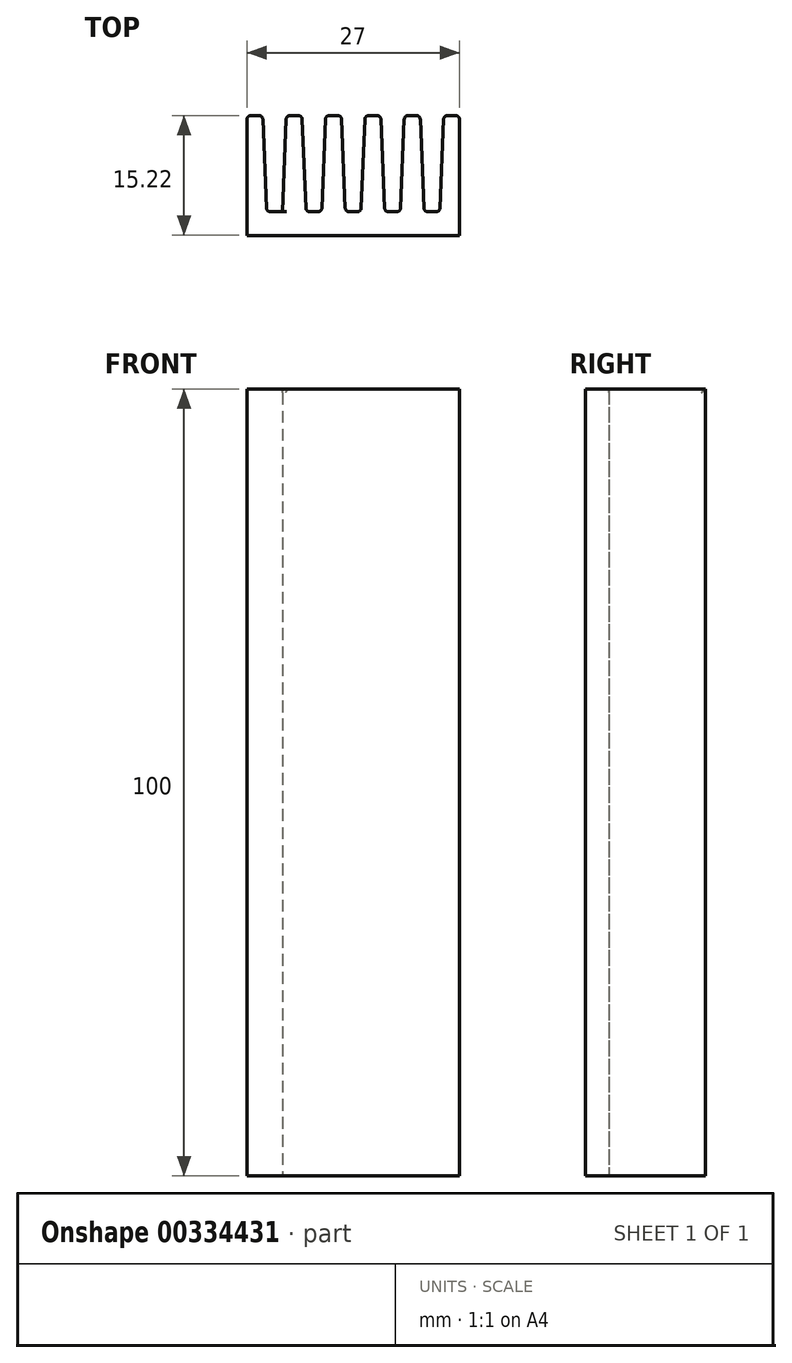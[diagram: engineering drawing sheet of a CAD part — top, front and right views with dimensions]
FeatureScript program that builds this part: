
annotation { "Feature Type Name" : "Feature", "Feature Type Description" : "" }
export const myFeature = defineFeature(function(context is Context, id is Id, definition is map)
    precondition{}
    {
        {
            var Q0;
            Q0=qCreatedBy(makeId("Top.planeOp"),FACE);
            var sketch = newSketch(context, id + "F0", { "sketchPlane" : qUnion([Q0])});
            skLineSegment(sketch, "E0", {"start": v(-38.74, 8.35) * mm, "end": v(-38.74, -6.87) * mm});
            skLineSegment(sketch, "E1", {"start": v(-38.74, 8.35) * mm, "end": v(-36.74, 8.35) * mm});
            skLineSegment(sketch, "E2", {"start": v(-36.74, 8.35) * mm, "end": v(-36.24, -3.87) * mm});
            skLineSegment(sketch, "E3", {"start": v(-36.24, -3.87) * mm, "end": v(-34.24, -3.87) * mm});
            skLineSegment(sketch, "E4", {"start": v(-34.24, -3.87) * mm, "end": v(-33.74, 8.35) * mm});
            skLineSegment(sketch, "E5", {"start": v(-33.74, 8.35) * mm, "end": v(-31.74, 8.35) * mm});
            skLineSegment(sketch, "E6.1.0.0", {"start": v(-28.74, 8.35) * mm, "end": v(-26.74, 8.35) * mm});
            skLineSegment(sketch, "E6.1.0.1", {"start": v(-29.24, -3.87) * mm, "end": v(-28.74, 8.35) * mm});
            skLineSegment(sketch, "E6.1.0.2", {"start": v(-31.24, -3.87) * mm, "end": v(-29.24, -3.87) * mm});
            skLineSegment(sketch, "E6.1.0.3", {"start": v(-31.74, 8.35) * mm, "end": v(-31.24, -3.87) * mm});
            skLineSegment(sketch, "E6.2.0.0", {"start": v(-23.74, 8.35) * mm, "end": v(-21.74, 8.35) * mm});
            skLineSegment(sketch, "E6.2.0.1", {"start": v(-24.24, -3.87) * mm, "end": v(-23.74, 8.35) * mm});
            skLineSegment(sketch, "E6.2.0.2", {"start": v(-26.24, -3.87) * mm, "end": v(-24.24, -3.87) * mm});
            skLineSegment(sketch, "E6.2.0.3", {"start": v(-26.74, 8.35) * mm, "end": v(-26.24, -3.87) * mm});
            skLineSegment(sketch, "E6.3.0.0", {"start": v(-18.74, 8.35) * mm, "end": v(-16.74, 8.35) * mm});
            skLineSegment(sketch, "E6.3.0.1", {"start": v(-19.24, -3.87) * mm, "end": v(-18.74, 8.35) * mm});
            skLineSegment(sketch, "E6.3.0.2", {"start": v(-21.24, -3.87) * mm, "end": v(-19.24, -3.87) * mm});
            skLineSegment(sketch, "E6.3.0.3", {"start": v(-21.74, 8.35) * mm, "end": v(-21.24, -3.87) * mm});
            skLineSegment(sketch, "E6.4.0.0", {"start": v(-13.74, 8.35) * mm, "end": v(-11.74, 8.35) * mm});
            skLineSegment(sketch, "E6.4.0.1", {"start": v(-14.24, -3.87) * mm, "end": v(-13.74, 8.35) * mm});
            skLineSegment(sketch, "E6.4.0.2", {"start": v(-16.24, -3.87) * mm, "end": v(-14.24, -3.87) * mm});
            skLineSegment(sketch, "E6.4.0.3", {"start": v(-16.74, 8.35) * mm, "end": v(-16.24, -3.87) * mm});
            skLineSegment(sketch, "E6.direction1", {"start": v(-36.24, -3.87) * mm, "end": v(-31.24, -3.87) * mm, "construction": true});
            skLineSegment(sketch, "E7", {"start": v(-11.74, 8.35) * mm, "end": v(-11.74, -6.87) * mm});
            skLineSegment(sketch, "E8", {"start": v(-11.74, -6.87) * mm, "end": v(-38.74, -6.87) * mm});
            skSolve(sketch);
        }
        {
            var Q0;
            Q0=makeQuery(id+"F0.imprint","IMPRINT",FACE,{"disambiguationData":[TD([[makeQuery(id+"F0.imprint","IMPRINT",EDGE,{"derivedFrom":sQuery(id+"F0.wireOp",EDGE,"E0")}),1.0]])]});
            extrude(context, id + "F1", {"entities" : qUnion([Q0]), "depth" : 100 * mm});
        }
        {
            var Q0;
            Q0=makeQuery(id+"F1.opExtrude","SWEPT_EDGE",EDGE,{"disambiguationData":[OSD([sQuery(id+"F0.wireOp",EDGE,"E6.4.0.0"),sQuery(id+"F0.wireOp",EDGE,"E6.4.0.1")])]});
            var Q1;
            Q1=makeQuery(id+"F1.opExtrude","SWEPT_EDGE",EDGE,{"disambiguationData":[OSD([sQuery(id+"F0.wireOp",EDGE,"E6.4.0.0"),sQuery(id+"F0.wireOp",EDGE,"E7")])]});
            var Q2;
            Q2=makeQuery(id+"F1.opExtrude","SWEPT_EDGE",EDGE,{"disambiguationData":[OSD([sQuery(id+"F0.wireOp",EDGE,"E6.3.0.0"),sQuery(id+"F0.wireOp",EDGE,"E6.3.0.1")])]});
            var Q3;
            Q3=makeQuery(id+"F1.opExtrude","SWEPT_EDGE",EDGE,{"disambiguationData":[OSD([sQuery(id+"F0.wireOp",EDGE,"E6.3.0.0"),sQuery(id+"F0.wireOp",EDGE,"E6.4.0.3")])]});
            var Q4;
            Q4=makeQuery(id+"F1.opExtrude","SWEPT_EDGE",EDGE,{"disambiguationData":[OSD([sQuery(id+"F0.wireOp",EDGE,"E6.2.0.0"),sQuery(id+"F0.wireOp",EDGE,"E6.2.0.1")])]});
            var Q5;
            Q5=makeQuery(id+"F1.opExtrude","SWEPT_EDGE",EDGE,{"disambiguationData":[OSD([sQuery(id+"F0.wireOp",EDGE,"E6.2.0.0"),sQuery(id+"F0.wireOp",EDGE,"E6.3.0.3")])]});
            var Q6;
            Q6=makeQuery(id+"F1.opExtrude","SWEPT_EDGE",EDGE,{"disambiguationData":[OSD([sQuery(id+"F0.wireOp",EDGE,"E6.1.0.0"),sQuery(id+"F0.wireOp",EDGE,"E6.1.0.1")])]});
            var Q7;
            Q7=makeQuery(id+"F1.opExtrude","SWEPT_EDGE",EDGE,{"disambiguationData":[OSD([sQuery(id+"F0.wireOp",EDGE,"E6.1.0.0"),sQuery(id+"F0.wireOp",EDGE,"E6.2.0.3")])]});
            var Q8;
            Q8=makeQuery(id+"F1.opExtrude","SWEPT_EDGE",EDGE,{"disambiguationData":[OSD([sQuery(id+"F0.wireOp",EDGE,"E4"),sQuery(id+"F0.wireOp",EDGE,"E5")])]});
            var Q9;
            Q9=makeQuery(id+"F1.opExtrude","SWEPT_EDGE",EDGE,{"disambiguationData":[OSD([sQuery(id+"F0.wireOp",EDGE,"E5"),sQuery(id+"F0.wireOp",EDGE,"E6.1.0.3")])]});
            var Q10;
            Q10=makeQuery(id+"F1.opExtrude","SWEPT_EDGE",EDGE,{"disambiguationData":[OSD([sQuery(id+"F0.wireOp",EDGE,"E0"),sQuery(id+"F0.wireOp",EDGE,"E1")])]});
            var Q11;
            Q11=makeQuery(id+"F1.opExtrude","SWEPT_EDGE",EDGE,{"disambiguationData":[OSD([sQuery(id+"F0.wireOp",EDGE,"E1"),sQuery(id+"F0.wireOp",EDGE,"E2")])]});
            var Q12;
            Q12=makeQuery(id+"F1.opExtrude","SWEPT_EDGE",EDGE,{"disambiguationData":[OSD([sQuery(id+"F0.wireOp",EDGE,"E2"),sQuery(id+"F0.wireOp",EDGE,"E3")])]});
            var Q13;
            Q13=makeQuery(id+"F1.opExtrude","CAP_EDGE",EDGE,{"disambiguationData":[OSD([sQuery(id+"F0.wireOp",EDGE,"E4")])],"isStart":false});
            var Q14;
            Q14=makeQuery(id+"F1.opExtrude","SWEPT_EDGE",EDGE,{"disambiguationData":[OSD([sQuery(id+"F0.wireOp",EDGE,"E6.1.0.2"),sQuery(id+"F0.wireOp",EDGE,"E6.1.0.3")])]});
            var Q15;
            Q15=makeQuery(id+"F1.opExtrude","SWEPT_EDGE",EDGE,{"disambiguationData":[OSD([sQuery(id+"F0.wireOp",EDGE,"E6.2.0.2"),sQuery(id+"F0.wireOp",EDGE,"E6.2.0.3")])]});
            var Q16;
            Q16=makeQuery(id+"F1.opExtrude","SWEPT_EDGE",EDGE,{"disambiguationData":[OSD([sQuery(id+"F0.wireOp",EDGE,"E6.2.0.1"),sQuery(id+"F0.wireOp",EDGE,"E6.2.0.2")])]});
            var Q17;
            Q17=makeQuery(id+"F1.opExtrude","SWEPT_EDGE",EDGE,{"disambiguationData":[OSD([sQuery(id+"F0.wireOp",EDGE,"E6.1.0.1"),sQuery(id+"F0.wireOp",EDGE,"E6.1.0.2")])]});
            var Q18;
            Q18=makeQuery(id+"F1.opExtrude","SWEPT_EDGE",EDGE,{"disambiguationData":[OSD([sQuery(id+"F0.wireOp",EDGE,"E6.3.0.2"),sQuery(id+"F0.wireOp",EDGE,"E6.3.0.3")])]});
            var Q19;
            Q19=makeQuery(id+"F1.opExtrude","SWEPT_EDGE",EDGE,{"disambiguationData":[OSD([sQuery(id+"F0.wireOp",EDGE,"E6.3.0.1"),sQuery(id+"F0.wireOp",EDGE,"E6.3.0.2")])]});
            var Q20;
            Q20=makeQuery(id+"F1.opExtrude","SWEPT_EDGE",EDGE,{"disambiguationData":[OSD([sQuery(id+"F0.wireOp",EDGE,"E6.4.0.2"),sQuery(id+"F0.wireOp",EDGE,"E6.4.0.3")])]});
            var Q21;
            Q21=makeQuery(id+"F1.opExtrude","SWEPT_EDGE",EDGE,{"disambiguationData":[OSD([sQuery(id+"F0.wireOp",EDGE,"E6.4.0.1"),sQuery(id+"F0.wireOp",EDGE,"E6.4.0.2")])]});
            fillet(context, id + "F2", {"entities" : qUnion([Q0, Q1, Q2, Q3, Q4, Q5, Q6, Q7, Q8, Q9, Q10, Q11, Q12, Q13, Q14, Q15, Q16, Q17, Q18, Q19, Q20, Q21]), "radius" : 0.5 * mm, "tangentPropagation" : true, "allowEdgeOverflow" : false});
        }
    });
